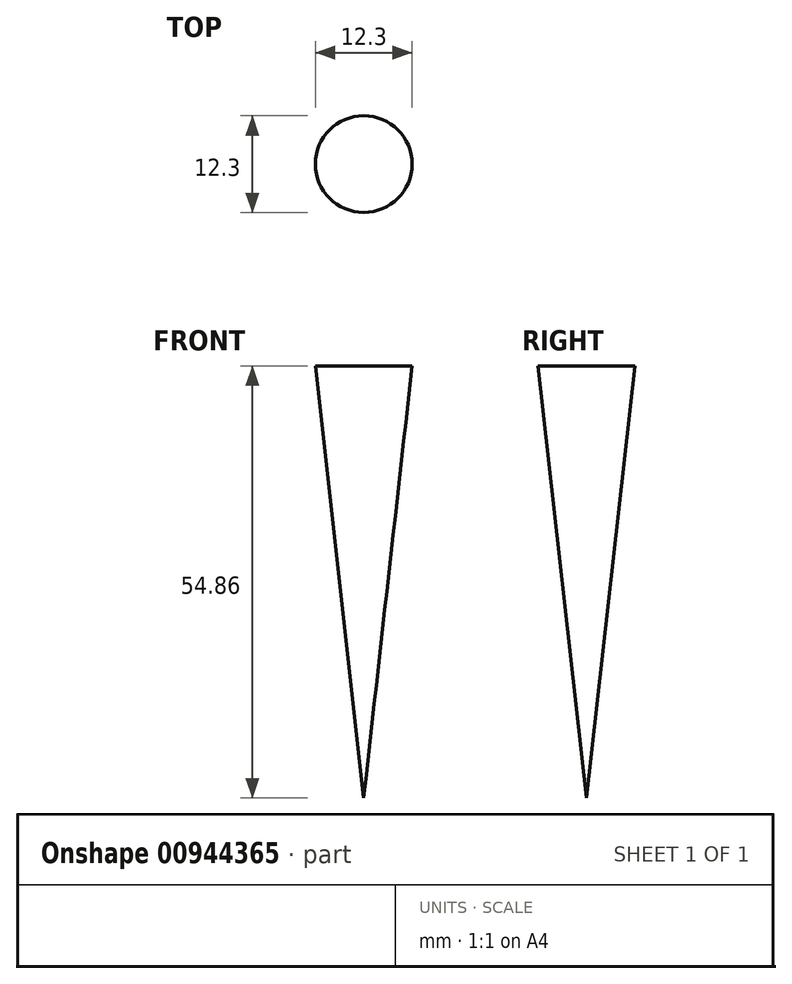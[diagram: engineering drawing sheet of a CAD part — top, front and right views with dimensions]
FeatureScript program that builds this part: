
annotation { "Feature Type Name" : "Feature", "Feature Type Description" : "" }
export const myFeature = defineFeature(function(context is Context, id is Id, definition is map)
    precondition{}
    {
        {
            var Q0;
            Q0=qCreatedBy(makeId("Top.planeOp"),FACE);
            var sketch = newSketch(context, id + "F0", { "sketchPlane" : qUnion([Q0])});
            skCircle(sketch, "E0", {"center": v(0, 0) * mm, "radius": 5.8 * mm});
            skSolve(sketch);
        }
        {
            var Q0;
            Q0=qCreatedBy(makeId("Top.planeOp"),FACE);
            cPlane(context, id + "F1", {"entities" : qUnion([Q0]), "cplaneType" : CPlaneType.OFFSET, "offset" : 54.86 * mm, "width" : 152.4 * mm, "height" : 152.4 * mm});
        }
        {
            var Q0;
            Q0=qCreatedBy(id+"F1.planeOp",FACE);
            var sketch = newSketch(context, id + "F2", { "sketchPlane" : qUnion([Q0])});
            skCircle(sketch, "E1", {"center": v(0, 0) * mm, "radius": 6.15 * mm});
            skSolve(sketch);
        }
        {
            var Q0;
            Q0=sQuery(id+"F2.wireOp",EDGE,"E1");
            var Q1;
            Q1=sQuery(id+"F0.wireOp",VERTEX,"E0.center");
            loft(context, id + "F3", {"bodyType" : ToolBodyType.SURFACE, "wireProfilesArray" : [{ "wireProfileEntities" : qUnion([Q0]) }, { "wireProfileEntities" : qUnion([Q1]) }]});
        }
        {
            var Q0;
            Q0=qCreatedBy(id+"F1.planeOp",FACE);
            cPlane(context, id + "F4", {"entities" : qUnion([Q0]), "cplaneType" : CPlaneType.OFFSET, "offset" : 33.02 * mm, "width" : 152.4 * mm, "height" : 152.4 * mm});
        }
    });
